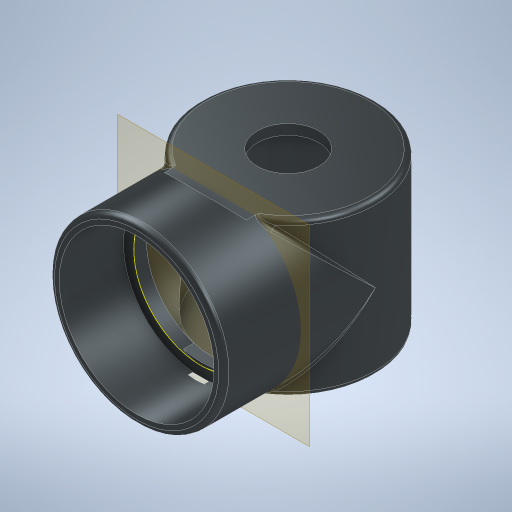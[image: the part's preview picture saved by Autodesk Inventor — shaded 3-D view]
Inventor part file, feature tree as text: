
AUTODESK INVENTOR PART (.ipt)
format: ipt  version: 2024 (Build 280153000, 153)  size: 483,840 bytes
history: native  units: mm
features: extrude x10, fillet x2, sketch x1, plane x1, projected_geometry x1
ambient origin geometry x8: Origin, YZ Plane, XZ Plane, XY Plane, X Axis, Y Axis, Z Axis, Center Point
bodies: Solid1 (feature_tree)
feature tree (15):
  extrude  "Extrusion1"  Depth=10.0mm
  extrude  "Extrusion2"  Depth=10.0mm TaperAngle=0.0deg
  sketch  "Sketch4"  dims[d0=60.325mm d1=68.0mm d2=19.05mm d3=0.0mm d4=68.0mm d5=40.0mm d6=4.0mm d7=52.0mm d8=0.0mm d11=52.0mm d12=0.0mm d13=4.0mm d14=0.0mm d15=4.0mm d16=0.0mm d17=25.0mm d18=25.0mm d19=61.0mm d20=0.0mm d21=-30.0mm d22=4.0mm d23=5.0mm d24=0.0mm d25=2.0mm d26=2.0mm d28=24.0mm d29=0.0mm d30=0.0mm d31=72.0mm d32=10.0mm d33=0.0mm d34=72.0mm d35=10.0mm d36=0.0mm]
  extrude  "Extrusion4"  Depth=10.0mm
  extrude  "Extrusion5"  Depth=10.0mm
  extrude  "Extrusion6"  Depth=10.0mm
  extrude  "Extrusion7"  Depth=10.0mm TaperAngle=0.0deg
  plane  "Work Plane1"
  extrude  "Extrusion8"  Depth=10.0mm TaperAngle=0.0deg
  fillet  "Fillet1"  Radius=4.0mm
  fillet  "Fillet2"  Radius=4.0mm
  extrude  "Extrusion9"  Depth=10.0mm
  extrude  "Extrusion10"  Depth=10.0mm
  extrude  "Extrusion11"  Depth=10.0mm TaperAngle=0.0deg
  projected_geometry  "Projected Loop1"
